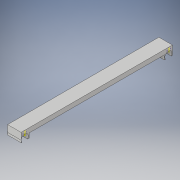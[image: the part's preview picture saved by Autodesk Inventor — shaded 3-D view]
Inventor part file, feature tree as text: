
AUTODESK INVENTOR PART (.ipt)
format: ipt  version: 2018 (Build 220112000, 112)  size: 267,264 bytes
history: native  units: in
note: dims shown in document units (in); Inventor stores cm internally (conversion verified against a paired STEP export)
features: sketch x7, extrude x4, hole x1
ambient origin geometry x8: Origin, YZ Plane, XZ Plane, XY Plane, X Axis, Y Axis, Z Axis, Center Point
bodies: Solid1 (feature_tree)
feature tree (12):
  extrude  "Extrusion1"  Depth=0.375in
  sketch  "Sketch2"  dims[d2=0.125in d3=0.0in d4=0.1in d5=0.0in]
  extrude  "Extrusion2"  Depth=0.1in TaperAngle=0.0deg
  sketch  "Sketch4"  dims[d9=0.22in d10=0.125in d11=0.0in]
  extrude  "Extrusion3"  Depth=0.22in
  extrude  "Extrusion4"  Depth=0.125in TaperAngle=0.0deg
  hole  "Hole1"  [1 undecoded]
  sketch  "Sketch1"  dims[d0=0.375in d1=4.0in]
  sketch  "Sketch3"  dims[d6=0.1in d7=0.0in d8=0.22in]
  sketch  "Sketch5"  dims[d12=0.2in]
  sketch  "Sketch6"  dims[d13=0.2in d14=0.75in d15=0.375in d16=0.25in d17=0.5635in d18=1.0in d19=0.8108in]
  sketch  "Sketch7"
note: 1 required parameter value undecoded (feature->parameter linkage not recoverable at this tier; creation-order binding heuristic only, values carry confidence <= 0.55)
